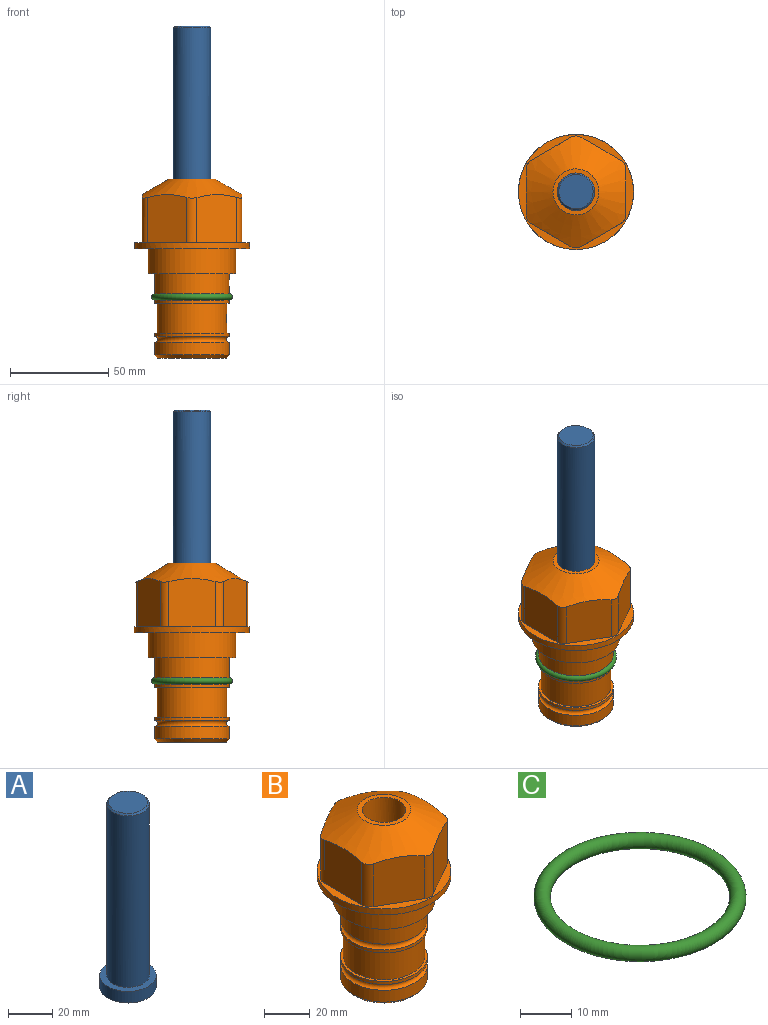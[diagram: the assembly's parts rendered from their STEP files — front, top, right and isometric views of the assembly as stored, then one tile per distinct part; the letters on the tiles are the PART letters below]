
ASSEMBLY  parts=3 mates=1
PART A: 6 faces, bbox 25.4x25.4x101.6 mm
  f0: plane 17.46x17.46mm, normal (0,0,1), area 239.5mm2, adj f5
  f1: plane 25.4x25.4mm, normal (0,0,-1), area 506.7mm2, adj f2
  f2: cylinder r=12.7mm len=25.4mm, axis (0,0,1), area 506.7mm2, adj f1,f3
  f3: plane 25.4x25.4mm, normal (0,0,1), area 221.7mm2, adj f2,f4
  f4: cylinder r=9.53mm len=94.46mm, axis (0,0,1), area 5653mm2, adj f3,f5
  f5: cone r=8.73mm half-angle=45deg, axis (0,0,-1), area 64.4mm2, adj f0,f4
PART B: 36 faces, bbox 58.7x58.7x91.2 mm
  f0: cylinder r=17.78mm len=35.56mm, axis (0,0,1), area 1670.8mm2, adj f23,f24,f31
  f1: cylinder r=19.05mm len=38.1mm, axis (0,0,1), area 1191.9mm2, adj f26,f27,f30
  f2: plane 58.66x58.66mm, normal (0,0,-1), area 1150.6mm2, adj f3,f28
  f3: cylinder r=29.33mm len=58.66mm, axis (0,0,-1), area 585.1mm2, adj f2,f4
  f4: plane 58.66x58.66mm, normal (0,0,1), area 475.9mm2, adj f3,f5,f6,f7,f8,f9,f10,f11
  f5: plane 24.5x20.32mm, normal (-0.5,0.87,0), area 562.8mm2, adj f4,f15,f16,f17
  f6: plane 24.5x20.32mm, normal (0.5,0.87,0), area 562.8mm2, adj f4,f14,f15,f17
  f7: plane 24.5x23.48mm, normal (1,0,0), area 562.8mm2, adj f4,f13,f14,f17
  f8: plane 24.5x20.32mm, normal (0.5,-0.87,0), area 562.8mm2, adj f4,f12,f13,f17
  f9: plane 24.5x20.32mm, normal (-0.5,-0.87,0), area 562.8mm2, adj f4,f11,f12,f17
  f10: plane 24.5x23.48mm, normal (-1,0,0), area 562.8mm2, adj f4,f11,f16,f17
  f11: cylinder r=5.08mm len=23.01mm, axis (0,0,-1), area 121.2mm2, adj f4,f9,f10,f17
  f12: cylinder r=5.08mm len=23.01mm, axis (0,0,-1), area 121.2mm2, adj f4,f8,f9,f17
  f13: cylinder r=5.08mm len=23.01mm, axis (0,0,-1), area 121.2mm2, adj f4,f7,f8,f17
  f14: cylinder r=5.08mm len=23.01mm, axis (0,0,-1), area 121.2mm2, adj f4,f6,f7,f17
  f15: cylinder r=5.08mm len=23.01mm, axis (0,0,-1), area 121.2mm2, adj f4,f5,f6,f17
  f16: cylinder r=5.08mm len=23.01mm, axis (0,0,-1), area 121.2mm2, adj f4,f5,f10,f17
  f17: cone r=11.73mm half-angle=60deg, axis (0,0,-1), area 2071.8mm2, adj f5,f6,f7,f8,f9,f10,f11,f12
  f18: plane 23.46x23.46mm, normal (0,0,1), area 147.4mm2, adj f17,f35
  f19: plane 34.93x34.93mm, normal (0,0,-1), area 958mm2, adj f29
  f20: cylinder r=19.05mm len=38.1mm, axis (0,0,1), area 760.1mm2, adj f21,f29
  f21: torus R=19.05mm, axis (0,0,1), area 565.3mm2, adj f20,f22
  f22: cylinder r=19.05mm len=38.1mm, axis (0,0,1), area 190mm2, adj f21,f23
  f23: plane 38.1x38.1mm, normal (0,0,1), area 146.9mm2, adj f0,f22
  f24: plane 38.1x38.1mm, normal (0,0,-1), area 146.9mm2, adj f0,f25
  f25: cylinder r=19.05mm len=38.1mm, axis (0,0,1), area 190mm2, adj f24,f26
  f26: torus R=19.05mm, axis (0,0,1), area 565.3mm2, adj f1,f25
  f27: plane 44.45x44.45mm, normal (0,0,-1), area 411.7mm2, adj f1,f28
  f28: cylinder r=22.23mm len=44.45mm, axis (0,0,1), area 1773.5mm2, adj f2,f27
  f29: cone r=19.05mm half-angle=45deg, axis (0,0,1), area 257.5mm2, adj f19,f20
  f30: cylinder r=3.17mm len=6.75mm, axis (-1,0,0), area 128mm2, adj f1,f33
  f31: cylinder r=3.17mm len=6.35mm, axis (-1,0,0), area 102.5mm2, adj f0,f33
  f32: plane 25.4x25.4mm, normal (0,0,1), area 506.7mm2, adj f33
  f33: cylinder r=12.7mm len=66.42mm, axis (0,0,-1), area 5236.2mm2, adj f30,f31,f32,f34
  f34: cone r=9.53mm half-angle=30deg, axis (0,0,-1), area 443.4mm2, adj f33,f35
  f35: cylinder r=9.53mm len=19.05mm, axis (0,0,-1), area 849mm2, adj f18,f34
PART C: 1 faces, bbox 44.7x44.7x3.2 mm
  f0: torus R=19.05mm, axis (0,0,1), area 1193.9mm2
PLACE A t=(0,0,39.92)mm
PLACE B at identity fixed
PLACE C at identity
MATE cylindrical A.f2 <-> B.f0  axis (0,0,1) through (0,0,65.56)mm
